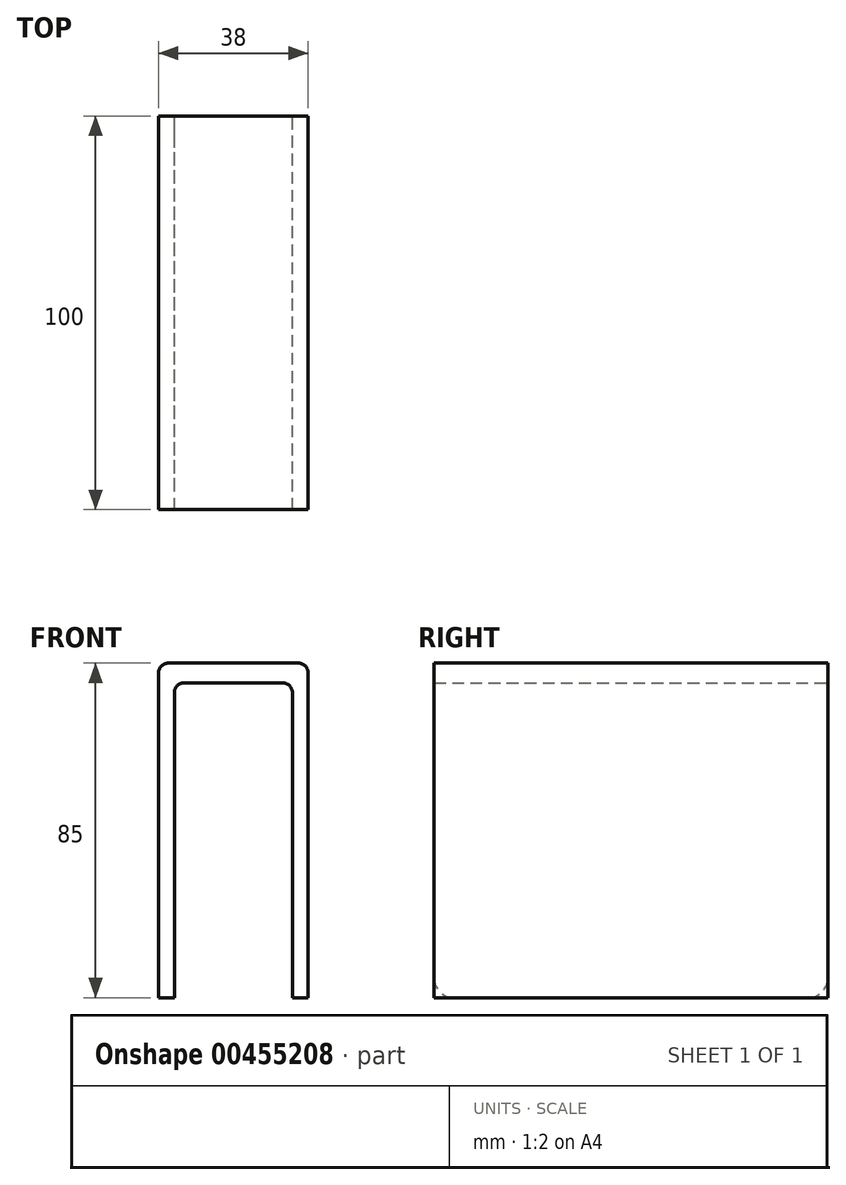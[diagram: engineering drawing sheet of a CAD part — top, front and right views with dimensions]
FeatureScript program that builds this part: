
annotation { "Feature Type Name" : "Feature", "Feature Type Description" : "" }
export const myFeature = defineFeature(function(context is Context, id is Id, definition is map)
    precondition{}
    {
        {
            var Q0;
            Q0=qCreatedBy(makeId("Front.planeOp"),FACE);
            var sketch = newSketch(context, id + "F0", { "sketchPlane" : qUnion([Q0])});
            skLineSegment(sketch, "E0", {"start": v(15.13, -39.94) * mm, "end": v(15.13, 37.56) * mm});
            skLineSegment(sketch, "E1", {"start": v(12.63, 40.06) * mm, "end": v(-12.37, 40.06) * mm});
            skLineSegment(sketch, "E2", {"start": v(-14.87, 37.56) * mm, "end": v(-14.87, -39.94) * mm});
            skLineSegment(sketch, "E3", {"start": v(19.13, -39.94) * mm, "end": v(19.13, 42.56) * mm});
            skLineSegment(sketch, "E4", {"start": v(-18.87, -39.94) * mm, "end": v(-18.87, 42.56) * mm});
            skLineSegment(sketch, "E5", {"start": v(0.13, 45.06) * mm, "end": v(16.63, 45.06) * mm});
            skPoint(sketch, "E5.startSnap0", {"position": v(0.13, 40.06) * mm});
            skLineSegment(sketch, "E6", {"start": v(0.13, 45.06) * mm, "end": v(-16.37, 45.06) * mm});
            skLineSegment(sketch, "E7", {"start": v(19.13, -39.94) * mm, "end": v(15.13, -39.94) * mm});
            skLineSegment(sketch, "E8", {"start": v(-14.87, -39.94) * mm, "end": v(-18.87, -39.94) * mm});
            skPoint(sketch, "E9.visualSharp", {"position": v(15.13, 40.06) * mm});
            skArc(sketch, "E9.filletArc", {"start": v(15.13, 37.56) * mm, "mid": v(14.4, 39.33) * mm, "end": v(12.63, 40.06) * mm});
            skPoint(sketch, "E10.visualSharp", {"position": v(-14.87, 40.06) * mm});
            skArc(sketch, "E10.filletArc", {"start": v(-12.37, 40.06) * mm, "mid": v(-14.14, 39.33) * mm, "end": v(-14.87, 37.56) * mm});
            skPoint(sketch, "E11.orphan", {"position": v(-18.87, 40.06) * mm});
            skPoint(sketch, "E12.visualSharp", {"position": v(-18.87, 45.06) * mm});
            skArc(sketch, "E12.filletArc", {"start": v(-16.37, 45.06) * mm, "mid": v(-18.14, 44.33) * mm, "end": v(-18.87, 42.56) * mm});
            skPoint(sketch, "E13.orphan", {"position": v(19.13, 40.06) * mm});
            skPoint(sketch, "E14.visualSharp", {"position": v(19.13, 45.06) * mm});
            skArc(sketch, "E14.filletArc", {"start": v(19.13, 42.56) * mm, "mid": v(18.4, 44.33) * mm, "end": v(16.63, 45.06) * mm});
            skSolve(sketch);
        }
        {
            var Q0;
            Q0=makeQuery(id+"F0.imprint","IMPRINT",FACE,{"disambiguationData":[TD([[makeQuery(id+"F0.imprint","IMPRINT",EDGE,{"derivedFrom":sQuery(id+"F0.wireOp",EDGE,"E0")}),-1.0]])]});
            extrude(context, id + "F1", {"entities" : qUnion([Q0]), "endBound" : BoundingType.SYMMETRIC, "depth" : 100 * mm});
        }
        {
            var Q0;
            Q0=makeQuery(id+"F1.opExtrude","CAP_EDGE",EDGE,{"disambiguationData":[OSD([sQuery(id+"F0.wireOp",EDGE,"E7")])],"isStart":false});
            var Q1;
            Q1=makeQuery(id+"F1.opExtrude","CAP_EDGE",EDGE,{"disambiguationData":[OSD([sQuery(id+"F0.wireOp",EDGE,"E8")])],"isStart":false});
            var Q2;
            Q2=makeQuery(id+"F1.opExtrude","CAP_EDGE",EDGE,{"disambiguationData":[OSD([sQuery(id+"F0.wireOp",EDGE,"E7")])],"isStart":true});
            var Q3;
            Q3=makeQuery(id+"F1.opExtrude","CAP_EDGE",EDGE,{"disambiguationData":[OSD([sQuery(id+"F0.wireOp",EDGE,"E8")])],"isStart":true});
            fillet(context, id + "F2", {"entities" : qUnion([Q0, Q1, Q2, Q3]), "radius" : 5 * mm, "tangentPropagation" : true, "allowEdgeOverflow" : false});
        }
    });
